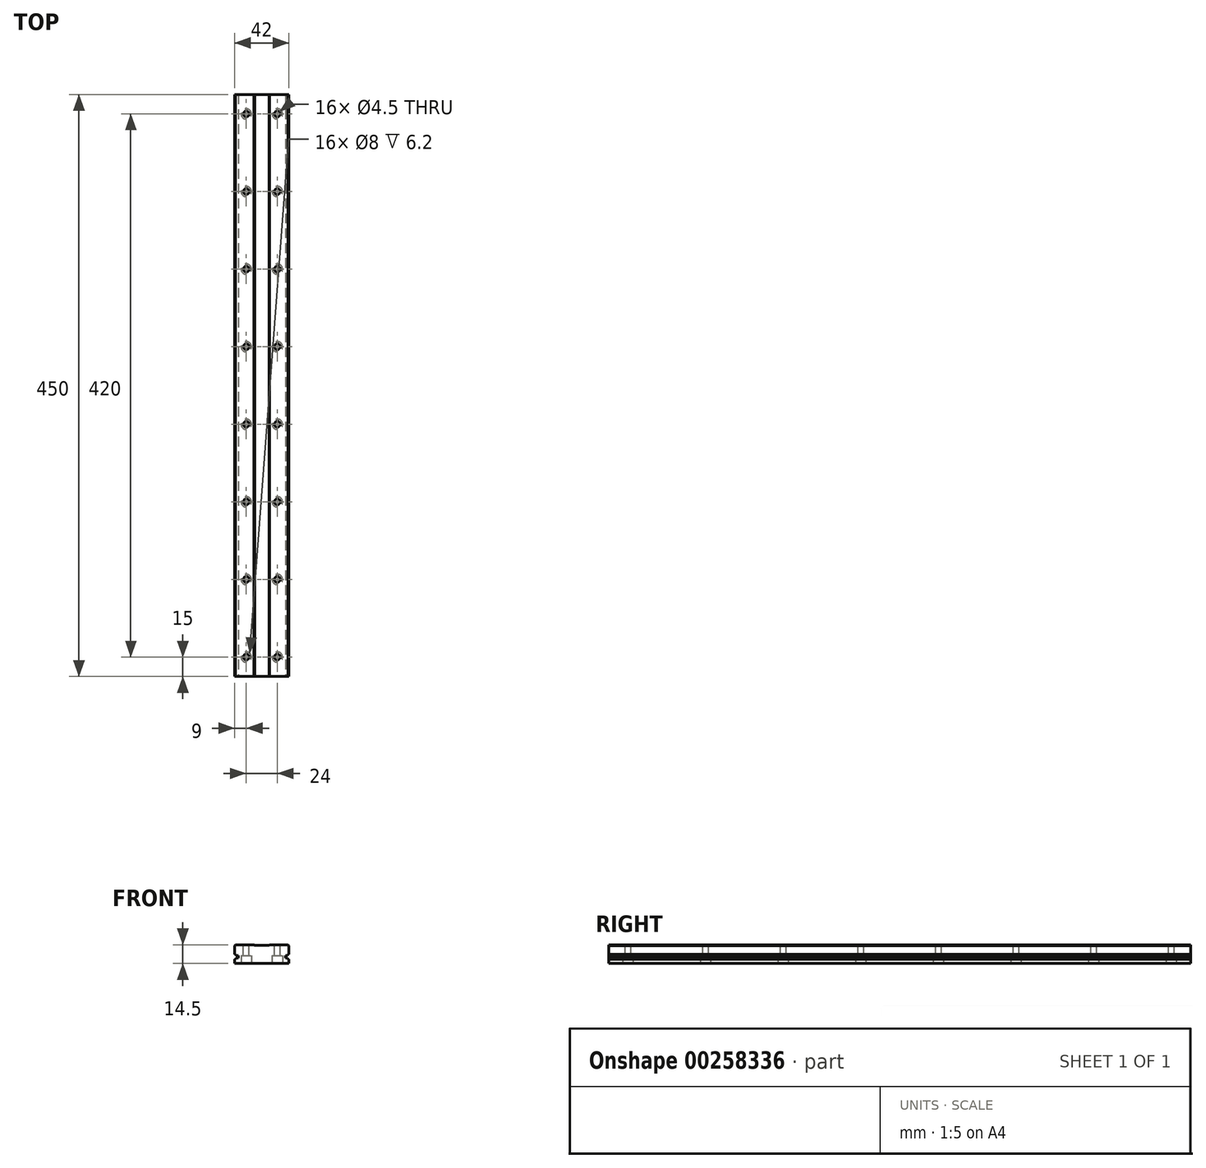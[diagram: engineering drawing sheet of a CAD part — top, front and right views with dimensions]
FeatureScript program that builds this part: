
annotation { "Feature Type Name" : "Feature", "Feature Type Description" : "" }
export const myFeature = defineFeature(function(context is Context, id is Id, definition is map)
    precondition{}
    {
        {
            var Q0;
            Q0=qCreatedBy(makeId("Front.planeOp"),FACE);
            var sketch = newSketch(context, id + "F0", { "sketchPlane" : qUnion([Q0])});
            skLineSegment(sketch, "E0", {"start": v(0, -7) * mm, "end": v(0, 7) * mm, "construction": true});
            skLineSegment(sketch, "E1", {"start": v(0, -7) * mm, "end": v(-21, -7) * mm});
            skLineSegment(sketch, "E2", {"start": v(-21, -7) * mm, "end": v(-21, -3.8) * mm});
            skLineSegment(sketch, "E3", {"start": v(-21, -3.8) * mm, "end": v(-21, -3.8) * mm});
            skLineSegment(sketch, "E4", {"start": v(-20, -2.8) * mm, "end": v(-20, -2.8) * mm});
            skLineSegment(sketch, "E5", {"start": v(-20, -2.8) * mm, "end": v(-18.2, -2.8) * mm});
            skLineSegment(sketch, "E6", {"start": v(-18.2, -2.8) * mm, "end": v(-18.2, -0.8) * mm});
            skLineSegment(sketch, "E7", {"start": v(-18.2, -0.8) * mm, "end": v(-20, -0.8) * mm});
            skLineSegment(sketch, "E8", {"start": v(-20, -0.8) * mm, "end": v(-20, -0.8) * mm});
            skLineSegment(sketch, "E9", {"start": v(-21, 0.2) * mm, "end": v(-21, 0.2) * mm});
            skLineSegment(sketch, "E10", {"start": v(-21, 0.2) * mm, "end": v(-21, 6.8) * mm});
            skLineSegment(sketch, "E11", {"start": v(-21, 6.8) * mm, "end": v(-20.3, 7.5) * mm});
            skLineSegment(sketch, "E12", {"start": v(-20.3, 7.5) * mm, "end": v(-6, 7.5) * mm});
            skLineSegment(sketch, "E13", {"start": v(-5.5, 7) * mm, "end": v(-6, 7.5) * mm});
            skLineSegment(sketch, "E14", {"start": v(-5.5, 7) * mm, "end": v(0, 7) * mm});
            skPoint(sketch, "E15.visualSharp", {"position": v(-20, -3.8) * mm});
            skArc(sketch, "E15.filletArc", {"start": v(-21, -3.8) * mm, "mid": v(-20.3, -3.5) * mm, "end": v(-20, -2.8) * mm});
            skPoint(sketch, "E16.visualSharp", {"position": v(-20, 0.2) * mm});
            skArc(sketch, "E16.filletArc", {"start": v(-20, -0.8) * mm, "mid": v(-20.3, -0.1) * mm, "end": v(-21, 0.2) * mm});
            skLineSegment(sketch, "E17", {"start": v(-18.2, -1.8) * mm, "end": v(-21, -1.8) * mm, "construction": true});
            skArc(sketch, "E18.MirrorCS", {"start": v(20, -0.8) * mm, "mid": v(20.3, -0.1) * mm, "end": v(21, 0.2) * mm});
            skArc(sketch, "E19.MirrorCS", {"start": v(21, -3.8) * mm, "mid": v(20.3, -3.5) * mm, "end": v(20, -2.8) * mm});
            skLineSegment(sketch, "E20.MirrorCS", {"start": v(5.5, 7) * mm, "end": v(6, 7.5) * mm});
            skLineSegment(sketch, "E21.MirrorCS", {"start": v(20, -2.8) * mm, "end": v(18.2, -2.8) * mm});
            skLineSegment(sketch, "E22.MirrorCS", {"start": v(18.2, -0.8) * mm, "end": v(20, -0.8) * mm});
            skLineSegment(sketch, "E23.MirrorCS", {"start": v(21, 6.8) * mm, "end": v(20.3, 7.5) * mm});
            skLineSegment(sketch, "E24.MirrorCS", {"start": v(18.2, -1.8) * mm, "end": v(21, -1.8) * mm, "construction": true});
            skLineSegment(sketch, "E25.MirrorCS", {"start": v(18.2, -2.8) * mm, "end": v(18.2, -0.8) * mm});
            skPoint(sketch, "E26.MirrorP", {"position": v(20, 0.2) * mm});
            skLineSegment(sketch, "E27.MirrorCS", {"start": v(0, -7) * mm, "end": v(21, -7) * mm});
            skPoint(sketch, "E28.MirrorP", {"position": v(20, -3.8) * mm});
            skLineSegment(sketch, "E29.MirrorCS", {"start": v(21, -7) * mm, "end": v(21, -3.8) * mm});
            skLineSegment(sketch, "E30.MirrorCS", {"start": v(5.5, 7) * mm, "end": v(0, 7) * mm});
            skLineSegment(sketch, "E31.MirrorCS", {"start": v(21, 0.2) * mm, "end": v(21, 0.2) * mm});
            skLineSegment(sketch, "E32.MirrorCS", {"start": v(21, -3.8) * mm, "end": v(21, -3.8) * mm});
            skLineSegment(sketch, "E33.MirrorCS", {"start": v(21, 0.2) * mm, "end": v(21, 6.8) * mm});
            skLineSegment(sketch, "E34.MirrorCS", {"start": v(20, -0.8) * mm, "end": v(20, -0.8) * mm});
            skLineSegment(sketch, "E35.MirrorCS", {"start": v(20.3, 7.5) * mm, "end": v(6, 7.5) * mm});
            skLineSegment(sketch, "E36.MirrorCS", {"start": v(20, -2.8) * mm, "end": v(20, -2.8) * mm});
            skSolve(sketch);
        }
        {
            var Q0;
            Q0=qSketchRegion(id+"F0",true);
            extrude(context, id + "F1", {"entities" : qUnion([Q0]), "oppositeDirection" : true, "depth" : 450 * mm});
        }
        {
            var Q0;
            Q0=makeQuery(id+"F1.opExtrude","SWEPT_FACE",FACE,{"disambiguationData":[OSD([sQuery(id+"F0.wireOp",EDGE,"E12")])]});
            var sketch = newSketch(context, id + "F2", { "sketchPlane" : qUnion([Q0])});
            skCircle(sketch, "E37", {"center": v(-12, 15) * mm, "radius": 2.25 * mm});
            skCircle(sketch, "E38", {"center": v(-12, 75) * mm, "radius": 2.25 * mm});
            skCircle(sketch, "E39", {"center": v(-12, 135) * mm, "radius": 2.25 * mm});
            skCircle(sketch, "E40", {"center": v(-12, 375) * mm, "radius": 2.25 * mm});
            skCircle(sketch, "E41", {"center": v(-12, 195) * mm, "radius": 2.25 * mm});
            skCircle(sketch, "E42", {"center": v(-12, 255) * mm, "radius": 2.25 * mm});
            skCircle(sketch, "E43", {"center": v(-12, 315) * mm, "radius": 2.25 * mm});
            skCircle(sketch, "E44", {"center": v(-12, 435) * mm, "radius": 2.25 * mm});
            skLineSegment(sketch, "E45", {"start": v(0, 0) * mm, "end": v(0, 450) * mm, "construction": true});
            skCircle(sketch, "E46.MirrorC", {"center": v(12, 15) * mm, "radius": 2.25 * mm});
            skCircle(sketch, "E47.MirrorC", {"center": v(12, 435) * mm, "radius": 2.25 * mm});
            skCircle(sketch, "E48.MirrorC", {"center": v(12, 315) * mm, "radius": 2.25 * mm});
            skCircle(sketch, "E49.MirrorC", {"center": v(12, 75) * mm, "radius": 2.25 * mm});
            skCircle(sketch, "E50.MirrorC", {"center": v(12, 135) * mm, "radius": 2.25 * mm});
            skCircle(sketch, "E51.MirrorC", {"center": v(12, 195) * mm, "radius": 2.25 * mm});
            skCircle(sketch, "E52.MirrorC", {"center": v(12, 255) * mm, "radius": 2.25 * mm});
            skCircle(sketch, "E53.MirrorC", {"center": v(12, 375) * mm, "radius": 2.25 * mm});
            skSolve(sketch);
        }
        {
            var Q0;
            Q0=qSketchRegion(id+"F2",true);
            extrude(context, id + "F3", {"entities" : qUnion([Q0]), "operationType" : NewBodyOperationType.REMOVE, "endBound" : BoundingType.UP_TO_NEXT, "oppositeDirection" : true, "depth" : 25 * mm});
        }
        {
            var Q0;
            Q0=makeQuery(id+"F1.opExtrude","SWEPT_FACE",FACE,{"disambiguationData":[OSD([sQuery(id+"F0.wireOp",EDGE,"E1"),sQuery(id+"F0.wireOp",EDGE,"E27.MirrorCS")])]});
            var sketch = newSketch(context, id + "F4", { "sketchPlane" : qUnion([Q0])});
            skCircle(sketch, "E54", {"center": v(-12, -435) * mm, "radius": 4 * mm});
            skCircle(sketch, "E55", {"center": v(12, -435) * mm, "radius": 4 * mm});
            skCircle(sketch, "E56", {"center": v(-12, -375) * mm, "radius": 4 * mm});
            skCircle(sketch, "E57", {"center": v(12, -375) * mm, "radius": 4 * mm});
            skCircle(sketch, "E58", {"center": v(-12, -315) * mm, "radius": 4 * mm});
            skCircle(sketch, "E59", {"center": v(12, -315) * mm, "radius": 4 * mm});
            skCircle(sketch, "E60", {"center": v(12, -255) * mm, "radius": 4 * mm});
            skCircle(sketch, "E61", {"center": v(-12, -255) * mm, "radius": 4 * mm});
            skCircle(sketch, "E62", {"center": v(-12, -195) * mm, "radius": 4 * mm});
            skCircle(sketch, "E63", {"center": v(12, -195) * mm, "radius": 4 * mm});
            skCircle(sketch, "E64", {"center": v(12, -135) * mm, "radius": 4 * mm});
            skCircle(sketch, "E65", {"center": v(-12, -75) * mm, "radius": 4 * mm});
            skCircle(sketch, "E66", {"center": v(-12, -135) * mm, "radius": 4 * mm});
            skCircle(sketch, "E67", {"center": v(12, -75) * mm, "radius": 4 * mm});
            skCircle(sketch, "E68", {"center": v(-12, -15) * mm, "radius": 4 * mm});
            skCircle(sketch, "E69", {"center": v(12, -15) * mm, "radius": 4 * mm});
            skSolve(sketch);
        }
        {
            var Q0;
            Q0=qSketchRegion(id+"F4",true);
            extrude(context, id + "F5", {"entities" : qUnion([Q0]), "operationType" : NewBodyOperationType.REMOVE, "oppositeDirection" : true, "depth" : 6.2 * mm});
        }
    });
